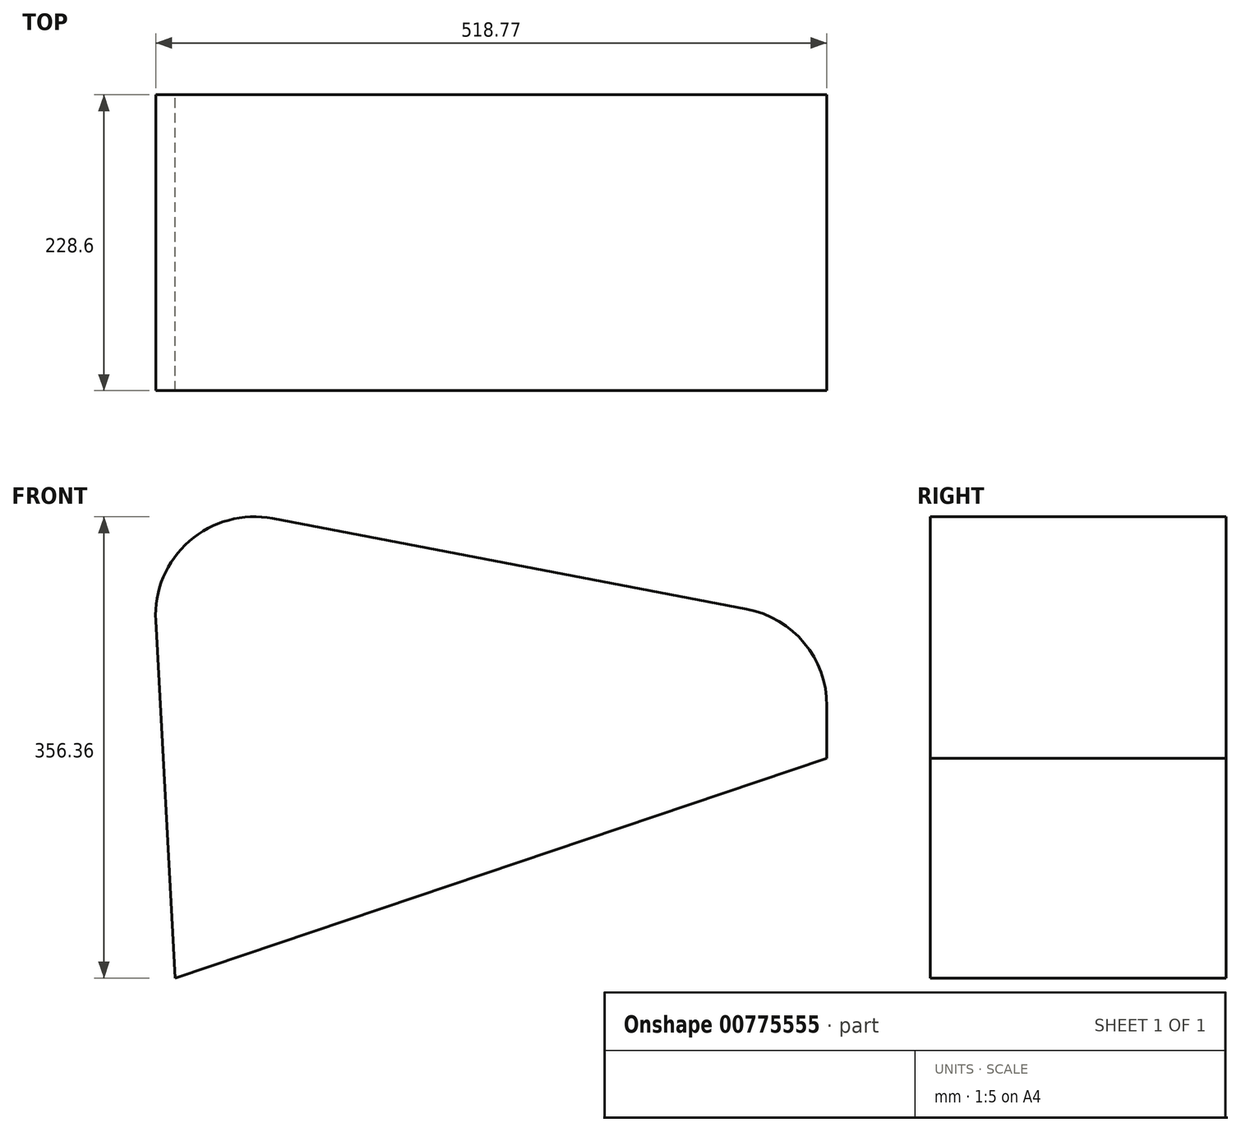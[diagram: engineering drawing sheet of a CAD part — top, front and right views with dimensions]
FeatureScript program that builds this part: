
annotation { "Feature Type Name" : "Feature", "Feature Type Description" : "" }
export const myFeature = defineFeature(function(context is Context, id is Id, definition is map)
    precondition{}
    {
        {
            var Q0;
            Q0=qCreatedBy(makeId("Front.planeOp"),FACE);
            var sketch = newSketch(context, id + "F0", { "sketchPlane" : qUnion([Q0])});
            skLineSegment(sketch, "E0", {"start": v(-259.45, 188.14) * mm, "end": v(264.48, 88.08) * mm});
            skLineSegment(sketch, "E1", {"start": v(264.48, 88.08) * mm, "end": v(264.48, -15.36) * mm});
            skLineSegment(sketch, "E2", {"start": v(264.48, -15.36) * mm, "end": v(-239.22, -185.13) * mm});
            skLineSegment(sketch, "E3", {"start": v(-239.22, -185.13) * mm, "end": v(-259.45, 188.14) * mm});
            skSolve(sketch);
        }
        {
            var Q0;
            Q0=makeQuery(id+"F0.imprint","IMPRINT",FACE,{"disambiguationData":[TD([[makeQuery(id+"F0.imprint","IMPRINT",EDGE,{"derivedFrom":sQuery(id+"F0.wireOp",EDGE,"E0")}),-1.0]])]});
            extrude(context, id + "F1", {"entities" : qUnion([Q0]), "depth" : 228.6 * mm, "offsetDistance" : 25.4 * mm});
        }
        {
            var Q0;
            Q0=makeQuery(id+"F1.opExtrude","SWEPT_EDGE",EDGE,{"disambiguationData":[OSD([sQuery(id+"F0.wireOp",EDGE,"E0"),sQuery(id+"F0.wireOp",EDGE,"E3")])]});
            var Q1;
            Q1=makeQuery(id+"F1.opExtrude","SWEPT_EDGE",EDGE,{"disambiguationData":[OSD([sQuery(id+"F0.wireOp",EDGE,"E0"),sQuery(id+"F0.wireOp",EDGE,"E1")])]});
            fillet(context, id + "F2", {"entities" : qUnion([Q0, Q1]), "radius" : 76.2 * mm, "tangentPropagation" : true, "allowEdgeOverflow" : false});
        }
    });
